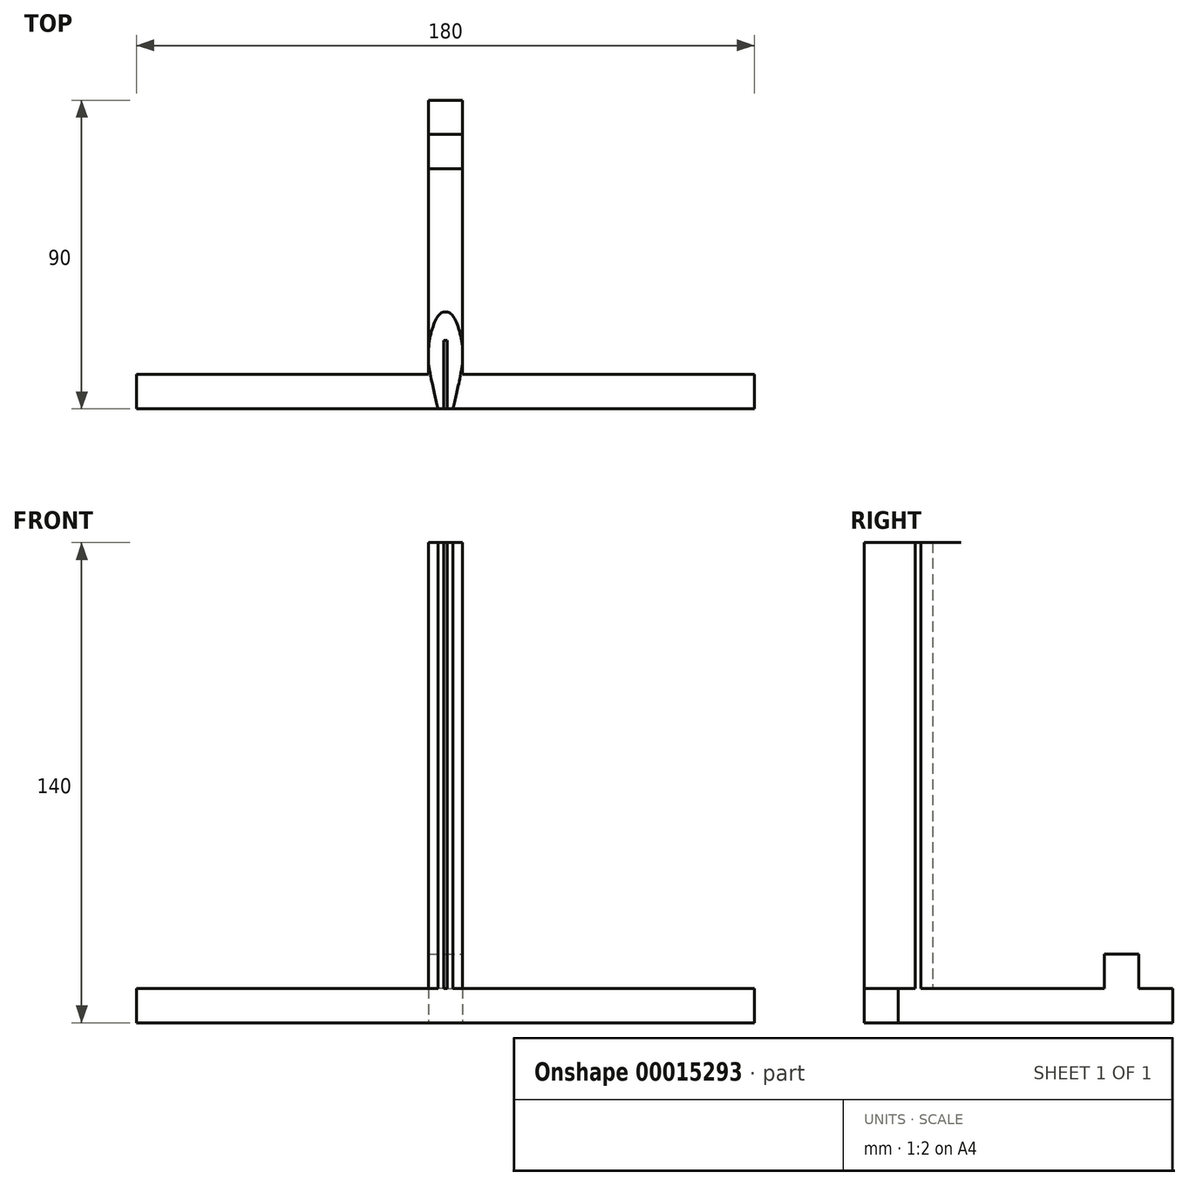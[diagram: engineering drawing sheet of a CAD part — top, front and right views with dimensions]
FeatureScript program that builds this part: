
annotation { "Feature Type Name" : "Feature", "Feature Type Description" : "" }
export const myFeature = defineFeature(function(context is Context, id is Id, definition is map)
    precondition{}
    {
        {
            var Q0;
            Q0=qCreatedBy(makeId("Top.planeOp"),FACE);
            var sketch = newSketch(context, id + "F0", { "sketchPlane" : qUnion([Q0])});
            skLineSegment(sketch, "E0", {"start": v(0, 90) * mm, "end": v(5, 90) * mm});
            skLineSegment(sketch, "E1", {"start": v(5, 90) * mm, "end": v(5, 10) * mm});
            skLineSegment(sketch, "E2", {"start": v(5, 10) * mm, "end": v(90, 10) * mm});
            skLineSegment(sketch, "E3", {"start": v(90, 10) * mm, "end": v(90, 0) * mm});
            skLineSegment(sketch, "E4", {"start": v(90, 0) * mm, "end": v(0, 0) * mm});
            skLineSegment(sketch, "E5.MirrorCS", {"start": v(0, 90) * mm, "end": v(-5, 90) * mm});
            skLineSegment(sketch, "E6.MirrorCS", {"start": v(-5, 90) * mm, "end": v(-5, 10) * mm});
            skLineSegment(sketch, "E7.MirrorCS", {"start": v(-5, 10) * mm, "end": v(-90, 10) * mm});
            skLineSegment(sketch, "E8.MirrorCS", {"start": v(-90, 10) * mm, "end": v(-90, 0) * mm});
            skLineSegment(sketch, "E9.MirrorCS", {"start": v(-90, 0) * mm, "end": v(0, 0) * mm});
            skSolve(sketch);
        }
        {
            var Q0;
            Q0=makeQuery(id+"F0.imprint","IMPRINT",FACE,{"disambiguationData":[TD([[makeQuery(id+"F0.imprint","IMPRINT",EDGE,{"derivedFrom":sQuery(id+"F0.wireOp",EDGE,"E0")}),-1.0]])]});
            extrude(context, id + "F1", {"entities" : qUnion([Q0]), "depth" : 10 * mm});
        }
        {
            var Q0;
            Q0=makeQuery(id+"F1.opExtrude","CAP_FACE",FACE,{"disambiguationData":[OSD([sQuery(id+"F0.wireOp",EDGE,"E0"),sQuery(id+"F0.wireOp",EDGE,"E1"),sQuery(id+"F0.wireOp",EDGE,"E2"),sQuery(id+"F0.wireOp",EDGE,"E3"),sQuery(id+"F0.wireOp",EDGE,"E4"),sQuery(id+"F0.wireOp",EDGE,"E5.MirrorCS"),sQuery(id+"F0.wireOp",EDGE,"E6.MirrorCS"),sQuery(id+"F0.wireOp",EDGE,"E7.MirrorCS"),sQuery(id+"F0.wireOp",EDGE,"E8.MirrorCS"),sQuery(id+"F0.wireOp",EDGE,"E9.MirrorCS")])],"isStart":false});
            var sketch = newSketch(context, id + "F2", { "sketchPlane" : qUnion([Q0])});
            skLineSegment(sketch, "E10.bottom", {"start": v(-5, 80) * mm, "end": v(5, 80) * mm});
            skLineSegment(sketch, "E10.top", {"start": v(-5, 70) * mm, "end": v(5, 70) * mm});
            skLineSegment(sketch, "E10.left", {"start": v(-5, 80) * mm, "end": v(-5, 70) * mm});
            skLineSegment(sketch, "E10.right", {"start": v(5, 80) * mm, "end": v(5, 70) * mm});
            skSolve(sketch);
        }
        {
            var Q0;
            Q0=makeQuery(id+"F2.imprint","IMPRINT",FACE,{"disambiguationData":[TD([[makeQuery(id+"F2.imprint","IMPRINT",EDGE,{"derivedFrom":sQuery(id+"F2.wireOp",EDGE,"E10.bottom")}),-1.0]])]});
            extrude(context, id + "F3", {"entities" : qUnion([Q0]), "operationType" : NewBodyOperationType.ADD, "depth" : 10 * mm});
        }
        {
            var Q0;
            {var subQ0=sQuery(id+"F0.wireOp",EDGE,"E1");var subQ1=sQuery(id+"F0.wireOp",EDGE,"E2");var subQ2=sQuery(id+"F0.wireOp",EDGE,"E3");var subQ3=sQuery(id+"F0.wireOp",EDGE,"E4");var subQ4=sQuery(id+"F0.wireOp",EDGE,"E6.MirrorCS");var subQ5=sQuery(id+"F0.wireOp",EDGE,"E7.MirrorCS");var subQ6=sQuery(id+"F0.wireOp",EDGE,"E8.MirrorCS");var subQ7=sQuery(id+"F0.wireOp",EDGE,"E9.MirrorCS");Q0=makeQuery(id+"F3.boolean.opBoolean","SPLIT",FACE,{"disambiguationData":[TD([makeQuery(id+"F1.opExtrude","SWEPT_FACE",FACE,{"disambiguationData":[OSD([subQ1])]})])],"derivedFrom":makeQuery(id+"F1.opExtrude","CAP_FACE",FACE,{"disambiguationData":[OSD([sQuery(id+"F0.wireOp",EDGE,"E0"),subQ0,subQ1,subQ2,subQ3,sQuery(id+"F0.wireOp",EDGE,"E5.MirrorCS"),subQ4,subQ5,subQ6,subQ7])],"isStart":false})});}
            var sketch = newSketch(context, id + "F4", { "sketchPlane" : qUnion([Q0])});
            skFitSpline(sketch, "E11", {"points": [v(0, 28.27) * mm, v(2.32, 26.82) * mm, v(5, 16.6) * mm, v(3.55, 6.02) * mm, v(2.2, 0) * mm], "startDerivative": vector(17.44, -0.09) * mm, "endDerivative": vector(-5.28, -21) * mm});
            skLineSegment(sketch, "E12", {"start": v(0, 28.27) * mm, "end": v(0, 24.79) * mm, "construction": true});
            skLineSegment(sketch, "E13", {"start": v(2.2, 0) * mm, "end": v(0.5, 0) * mm});
            skLineSegment(sketch, "E14", {"start": v(0.5, 0) * mm, "end": v(0.5, 20) * mm});
            skLineSegment(sketch, "E15", {"start": v(0.5, 20) * mm, "end": v(0, 20) * mm});
            skFitSpline(sketch, "E16.MirrorCS", {"points": [v(0, 28.27) * mm, v(-2.32, 26.82) * mm, v(-5, 16.6) * mm, v(-3.55, 6.02) * mm, v(-2.2, 0) * mm], "startDerivative": vector(-17.44, -0.09) * mm, "endDerivative": vector(5.28, -21) * mm});
            skLineSegment(sketch, "E17.MirrorCS", {"start": v(-0.5, 20) * mm, "end": v(0, 20) * mm});
            skLineSegment(sketch, "E18.MirrorCS", {"start": v(-0.5, 0) * mm, "end": v(-0.5, 20) * mm});
            skLineSegment(sketch, "E19.MirrorCS", {"start": v(-2.2, 0) * mm, "end": v(-0.5, 0) * mm});
            skSolve(sketch);
        }
        {
            var Q0;
            {var subQ19=sQuery(id+"F4.wireOp",EDGE,"E13");Q0=makeQuery(id+"F4.imprint","IMPRINT",FACE,{"disambiguationData":[TD([[makeQuery(id+"F4.imprint","IMPRINT",EDGE,{"derivedFrom":subQ19}),1.0]])]});}
            extrude(context, id + "F5", {"entities" : qUnion([Q0]), "operationType" : NewBodyOperationType.ADD, "depth" : 130 * mm});
        }
    });
